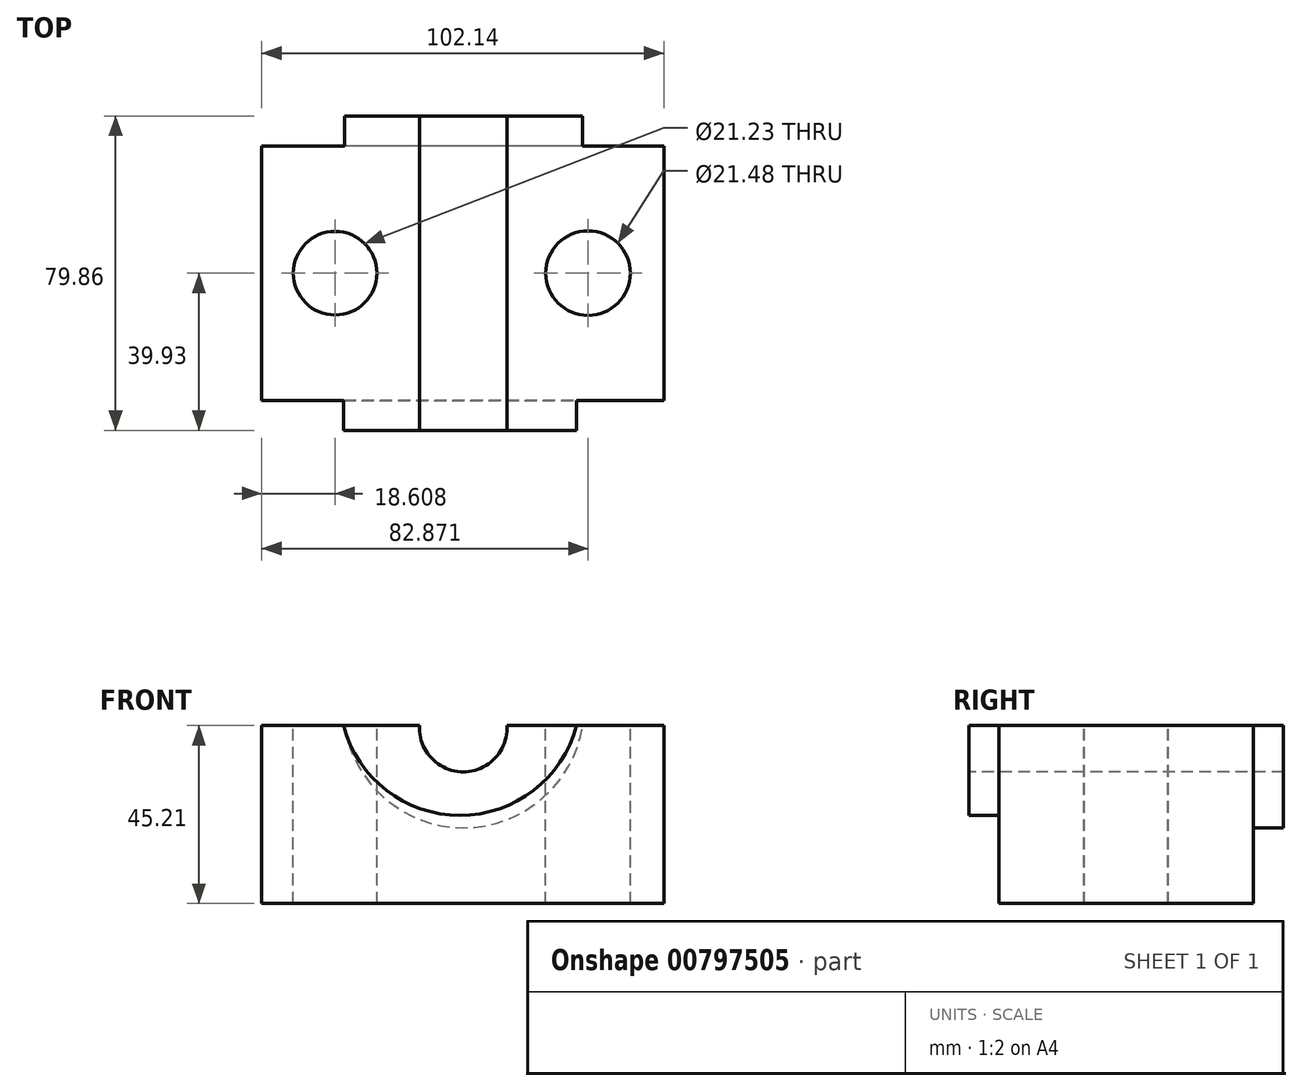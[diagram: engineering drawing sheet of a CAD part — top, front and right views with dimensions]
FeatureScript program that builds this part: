
annotation { "Feature Type Name" : "Feature", "Feature Type Description" : "" }
export const myFeature = defineFeature(function(context is Context, id is Id, definition is map)
    precondition{}
    {
        {
            var Q0;
            Q0=qCreatedBy(makeId("Top.planeOp"),FACE);
            var sketch = newSketch(context, id + "F0", { "sketchPlane" : qUnion([Q0])});
            skLineSegment(sketch, "E0.bottom", {"start": v(51.07, 39.93) * mm, "end": v(-51.07, 39.93) * mm});
            skLineSegment(sketch, "E0.top", {"start": v(51.07, -39.93) * mm, "end": v(-51.07, -39.93) * mm});
            skLineSegment(sketch, "E0.left", {"start": v(51.07, 39.93) * mm, "end": v(51.07, -39.93) * mm});
            skLineSegment(sketch, "E0.right", {"start": v(-51.07, 39.93) * mm, "end": v(-51.07, -39.93) * mm});
            skPoint(sketch, "E0.middle", {"position": v(0, 0) * mm});
            skSolve(sketch);
        }
        {
            var Q0;
            Q0 = qSketchRegion(id + "F0", true);
            var Q1;
            Q1=makeQuery(id+"F0.imprint","IMPRINT",FACE,{"disambiguationData":[TD([[makeQuery(id+"F0.imprint","IMPRINT",EDGE,{"derivedFrom":sQuery(id+"F0.wireOp",EDGE,"E0.bottom")}),1.0]])]});
            extrude(context, id + "F1", {"entities" : qUnion([Q0, Q1]), "depth" : 45.2 * mm, "offsetDistance" : 25.4 * mm});
        }
        {
            var Q0;
            Q0=makeQuery(id+"F1.opExtrude","SWEPT_FACE",FACE,{"disambiguationData":[OSD([sQuery(id+"F0.wireOp",EDGE,"E0.bottom")])]});
            var sketch = newSketch(context, id + "F2", { "sketchPlane" : qUnion([Q0])});
            skArc(sketch, "E1", {"start": v(-30.42, 45.21) * mm, "mid": v(-0.18, 19.25) * mm, "end": v(30.07, 45.21) * mm});
            skSolve(sketch);
        }
        {
            var Q0;
            {var subQ3=sQuery(id+"F2.wireOp",EDGE,"E1");Q0=makeQuery(id+"F2.imprint","IMPRINT",FACE,{"disambiguationData":[TD([[makeQuery(id+"F2.imprint","IMPRINT",EDGE,{"derivedFrom":subQ3}),-1.0]])]});}
            extrude(context, id + "F3", {"entities" : qUnion([Q0]), "operationType" : NewBodyOperationType.REMOVE, "oppositeDirection" : true, "depth" : 7.62 * mm, "offsetDistance" : 25.4 * mm});
        }
        {
            var Q0;
            Q0=makeQuery(id+"F1.opExtrude","SWEPT_FACE",FACE,{"disambiguationData":[OSD([sQuery(id+"F0.wireOp",EDGE,"E0.top")])]});
            var sketch = newSketch(context, id + "F4", { "sketchPlane" : qUnion([Q0])});
            skArc(sketch, "E2", {"start": v(-30.32, 45.21) * mm, "mid": v(-0.72, 22.38) * mm, "end": v(28.88, 45.21) * mm});
            skSolve(sketch);
        }
        {
            var Q0;
            {var subQ3=sQuery(id+"F4.wireOp",EDGE,"E2");Q0=makeQuery(id+"F4.imprint","IMPRINT",FACE,{"disambiguationData":[TD([[makeQuery(id+"F4.imprint","IMPRINT",EDGE,{"derivedFrom":subQ3}),-1.0]])]});}
            extrude(context, id + "F5", {"entities" : qUnion([Q0]), "operationType" : NewBodyOperationType.REMOVE, "oppositeDirection" : true, "depth" : 7.62 * mm, "offsetDistance" : 25.4 * mm});
        }
        {
            var Q0;
            Q0=makeQuery(id+"F1.opExtrude","CAP_FACE",FACE,{"disambiguationData":[OSD([sQuery(id+"F0.wireOp",EDGE,"E0.bottom"),sQuery(id+"F0.wireOp",EDGE,"E0.top"),sQuery(id+"F0.wireOp",EDGE,"E0.left"),sQuery(id+"F0.wireOp",EDGE,"E0.right")])],"isStart":false});
            var sketch = newSketch(context, id + "F6", { "sketchPlane" : qUnion([Q0])});
            skLineSegment(sketch, "E3.bottom", {"start": v(10.98, 39.93) * mm, "end": v(-10.98, 39.93) * mm});
            skLineSegment(sketch, "E3.top", {"start": v(10.98, -39.93) * mm, "end": v(-10.98, -39.93) * mm});
            skLineSegment(sketch, "E3.left", {"start": v(10.98, 39.93) * mm, "end": v(10.98, -39.93) * mm});
            skLineSegment(sketch, "E3.right", {"start": v(-10.98, 39.93) * mm, "end": v(-10.98, -39.93) * mm});
            skPoint(sketch, "E3.middle", {"position": v(0, 0) * mm});
            skSolve(sketch);
        }
        {
            var Q0;
            Q0=makeQuery(id+"F1.opExtrude","SWEPT_FACE",FACE,{"disambiguationData":[OSD([sQuery(id+"F0.wireOp",EDGE,"E0.top")])]});
            var sketch = newSketch(context, id + "F7", { "sketchPlane" : qUnion([Q0])});
            skArc(sketch, "E4", {"start": v(-11, 45.21) * mm, "mid": v(0.1, 33.45) * mm, "end": v(11.2, 45.21) * mm});
            skSolve(sketch);
        }
        {
            var Q0;
            {var subQ0=sQuery(id+"F7.wireOp",EDGE,"E4");Q0=makeQuery(id+"F7.imprint","IMPRINT",FACE,{"disambiguationData":[TD([[makeQuery(id+"F7.imprint","IMPRINT",EDGE,{"derivedFrom":subQ0}),1.0]])]});}
            extrude(context, id + "F8", {"entities" : qUnion([Q0]), "operationType" : NewBodyOperationType.REMOVE, "oppositeDirection" : true, "depth" : 240.8 * mm, "offsetDistance" : 25.4 * mm});
        }
        {
            var Q0;
            {var subQ12=sQuery(id+"F6.wireOp",EDGE,"E3.right");Q0=makeQuery(id+"F6.imprint","IMPRINT",FACE,{"disambiguationData":[TD([[makeQuery(id+"F6.imprint","IMPRINT",EDGE,{"derivedFrom":subQ12}),-1.0]])]});}
            var sketch = newSketch(context, id + "F9", { "sketchPlane" : qUnion([Q0])});
            skCircle(sketch, "E5", {"center": v(-32.46, 0) * mm, "radius": 10.61 * mm});
            skCircle(sketch, "E6", {"center": v(31.8, 0) * mm, "radius": 10.74 * mm});
            skSolve(sketch);
        }
        {
            var Q0;
            Q0 = qSketchRegion(id + "F9", true);
            extrude(context, id + "F10", {"entities" : qUnion([Q0]), "operationType" : NewBodyOperationType.REMOVE, "oppositeDirection" : true, "depth" : 83.57 * mm, "offsetDistance" : 25.4 * mm});
        }
    });
